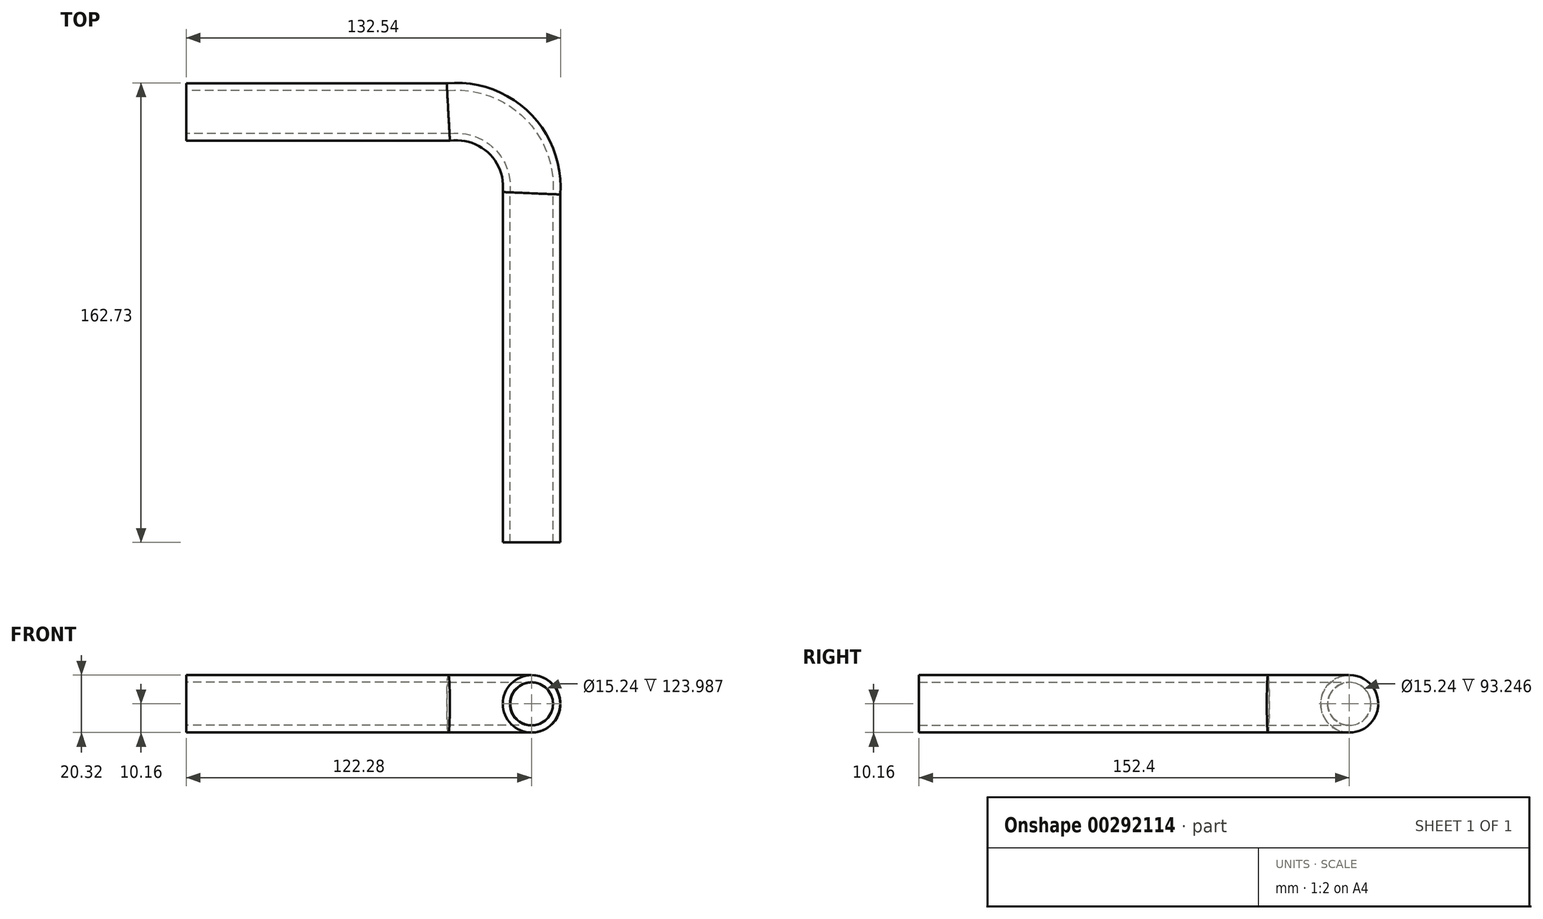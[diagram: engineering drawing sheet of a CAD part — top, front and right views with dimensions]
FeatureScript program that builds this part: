
annotation { "Feature Type Name" : "Feature", "Feature Type Description" : "" }
export const myFeature = defineFeature(function(context is Context, id is Id, definition is map)
    precondition{}
    {
        {
            var Q0;
            Q0=qCreatedBy(makeId("Top.planeOp"),FACE);
            var sketch = newSketch(context, id + "F0", { "sketchPlane" : qUnion([Q0])});
            skArc(sketch, "E0", {"start": v(0, 123.65) * mm, "mid": v(-7.92, 145) * mm, "end": v(-29.47, 152.4) * mm});
            skLineSegment(sketch, "E1", {"start": v(-122.28, 152.4) * mm, "end": v(-29.47, 152.4) * mm});
            skLineSegment(sketch, "E2", {"start": v(0, 123.65) * mm, "end": v(0, 0) * mm});
            skSolve(sketch);
        }
        {
            var Q0;
            Q0=qCreatedBy(makeId("Front.planeOp"),FACE);
            var sketch = newSketch(context, id + "F1", { "sketchPlane" : qUnion([Q0])});
            skCircle(sketch, "E3", {"center": v(0, 0) * mm, "radius": 7.62 * mm});
            skCircle(sketch, "E4", {"center": v(0, 0) * mm, "radius": 10.16 * mm});
            skSolve(sketch);
        }
        {
            var Q0;
            Q0=makeQuery(id+"F1.imprint","IMPRINT",FACE,{"disambiguationData":[TD([[makeQuery(id+"F1.imprint","IMPRINT",EDGE,{"derivedFrom":sQuery(id+"F1.wireOp",EDGE,"E3")}),-1.0]])]});
            var Q1;
            Q1=sQuery(id+"F0.wireOp",EDGE,"E2");
            var Q2;
            Q2=sQuery(id+"F0.wireOp",EDGE,"E0");
            var Q3;
            Q3=sQuery(id+"F0.wireOp",EDGE,"E1");
            var Q4;
            Q4=sQuery(id+"F0.wireOp",EDGE,"xcwwB5oc-PneU-uZ9Q-msC6-WU9smJogd8up");
            var Q5;
            Q5=sQuery(id+"F0.wireOp",EDGE,"FhEEhzaf-u9NL-Qos4-zuCU-yqp9chtstswA");
            sweep(context, id + "F2", {"profiles" : qUnion([Q0]), "path" : qUnion([Q1, Q2, Q3, Q4, Q5])});
        }
    });
